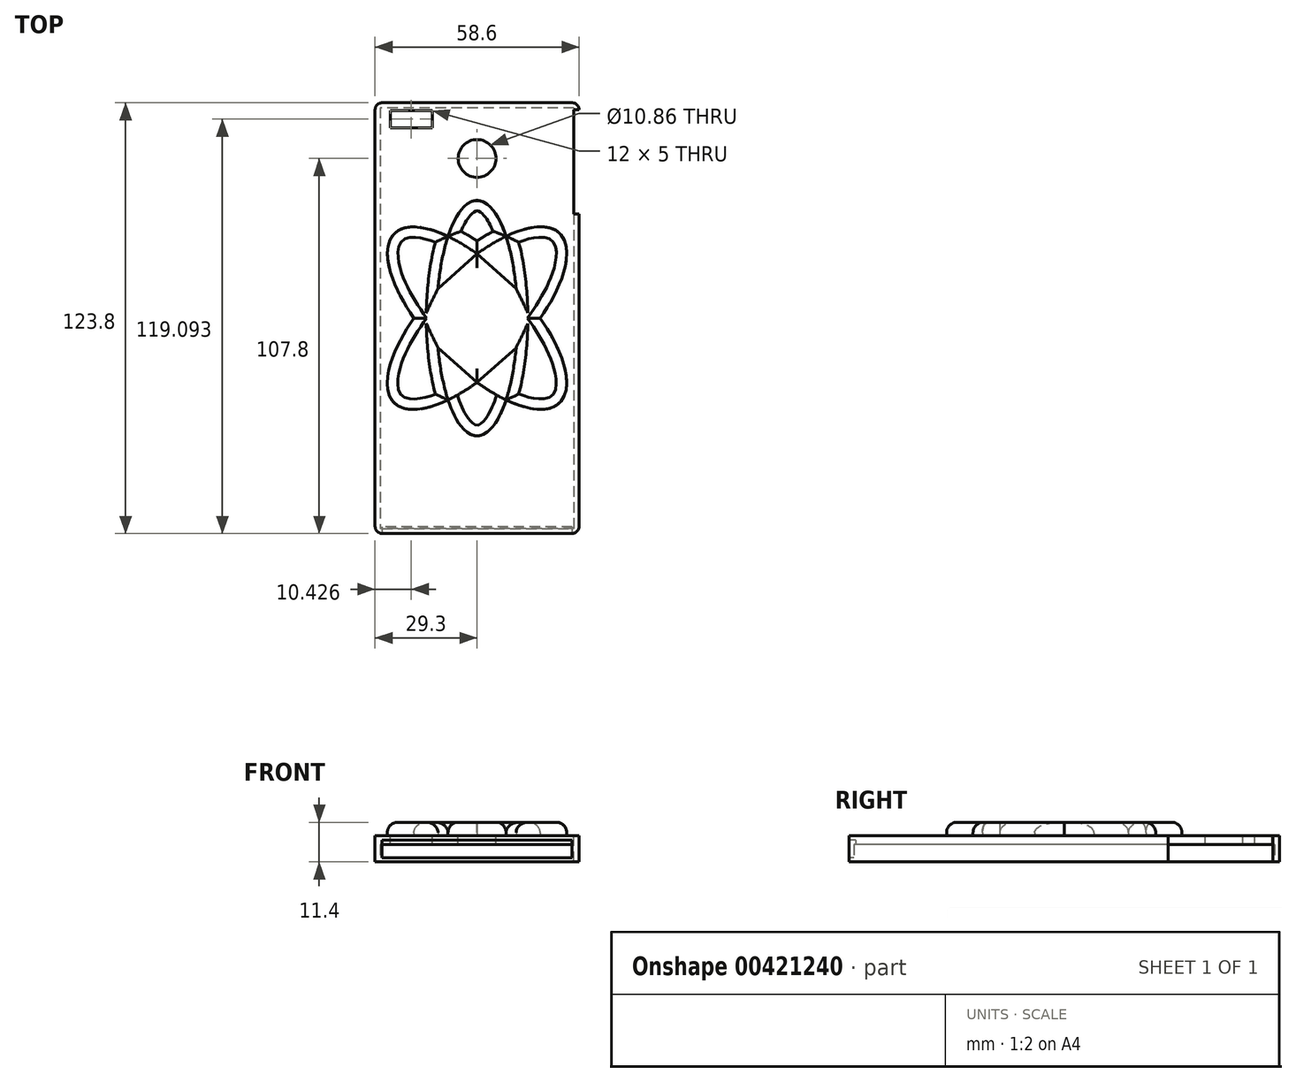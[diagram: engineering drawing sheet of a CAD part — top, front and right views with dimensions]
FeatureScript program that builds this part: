
annotation { "Feature Type Name" : "Feature", "Feature Type Description" : "" }
export const myFeature = defineFeature(function(context is Context, id is Id, definition is map)
    precondition{}
    {
        {
            var Q0;
            Q0=qCreatedBy(makeId("Top.planeOp"),FACE);
            var sketch = newSketch(context, id + "F0", { "sketchPlane" : qUnion([Q0])});
            skLineSegment(sketch, "E0", {"start": v(0, 0) * mm, "end": v(0, 69.75) * mm});
            skLineSegment(sketch, "E1", {"start": v(0, 0) * mm, "end": v(0, -69.75) * mm});
            skLineSegment(sketch, "E2", {"start": v(0, 0) * mm, "end": v(-58.6, 0) * mm});
            skLineSegment(sketch, "E3", {"start": v(0, 0) * mm, "end": v(70.03, 0) * mm});
            skLineSegment(sketch, "E4", {"start": v(70.03, 0) * mm, "end": v(70.03, 69.75) * mm});
            skLineSegment(sketch, "E5", {"start": v(0, 69.75) * mm, "end": v(70.03, 69.75) * mm});
            skLineSegment(sketch, "E6", {"start": v(70.03, 0) * mm, "end": v(70.03, -69.75) * mm});
            skLineSegment(sketch, "E7", {"start": v(70.03, -69.75) * mm, "end": v(0, -69.75) * mm});
            skLineSegment(sketch, "E8", {"start": v(0, -69.75) * mm, "end": v(-58.6, -69.75) * mm});
            skLineSegment(sketch, "E9", {"start": v(-58.6, -69.75) * mm, "end": v(-58.6, 0) * mm});
            skLineSegment(sketch, "E10", {"start": v(-58.6, 0) * mm, "end": v(-58.6, 69.75) * mm});
            skLineSegment(sketch, "E11", {"start": v(-58.6, 69.75) * mm, "end": v(0, 69.75) * mm});
            skLineSegment(sketch, "E12", {"start": v(-29.3, 0) * mm, "end": v(-29.3, 61.9) * mm});
            skLineSegment(sketch, "E13", {"start": v(-29.3, 0) * mm, "end": v(-29.3, -61.9) * mm});
            skLineSegment(sketch, "E14", {"start": v(-29.3, -61.9) * mm, "end": v(0, -61.9) * mm});
            skLineSegment(sketch, "E15", {"start": v(0, -61.9) * mm, "end": v(29.3, -61.9) * mm});
            skLineSegment(sketch, "E16", {"start": v(29.3, -61.9) * mm, "end": v(29.3, 61.9) * mm});
            skLineSegment(sketch, "E17", {"start": v(29.3, 61.9) * mm, "end": v(-29.3, 61.9) * mm});
            skSolve(sketch);
        }
        {
            var Q0;
            {var subQ4=sQuery(id+"F0.wireOp",EDGE,"E13");Q0=makeQuery(id+"F0.imprint","IMPRINT",FACE,{"disambiguationData":[TD([[makeQuery(id+"F0.imprint","IMPRINT",EDGE,{"derivedFrom":subQ4}),1.0]])]});}
            var Q1;
            {var subQ3=sQuery(id+"F0.wireOp",EDGE,"E15");Q1=makeQuery(id+"F0.imprint","IMPRINT",FACE,{"disambiguationData":[TD([[makeQuery(id+"F0.imprint","IMPRINT",EDGE,{"derivedFrom":subQ3}),1.0]])]});}
            var Q2;
            {var subQ3=sQuery(id+"F0.wireOp",EDGE,"E17");var subQ5=sQuery(id+"F0.wireOp",EDGE,"E16");var subQ7=makeQuery(id+"F0.imprint","INTERSECT",VERTEX,{"derivedFrom":[subQ5,subQ3]});Q2=makeQuery(id+"F0.imprint","IMPRINT",FACE,{"disambiguationData":[TD([[makeQuery(id+"F0.imprint","IMPRINT",EDGE,{"disambiguationData":[TD([[subQ7,1.0]])],"derivedFrom":subQ5}),1.0]])]});}
            var Q3;
            {var subQ5=sQuery(id+"F0.wireOp",EDGE,"E12");Q3=makeQuery(id+"F0.imprint","IMPRINT",FACE,{"disambiguationData":[TD([[makeQuery(id+"F0.imprint","IMPRINT",EDGE,{"derivedFrom":subQ5}),-1.0]])]});}
            extrude(context, id + "F1", {"entities" : qUnion([Q0, Q1, Q2, Q3]), "depth" : 7.6 * mm});
        }
        {
            var Q0;
            Q0=makeQuery(id+"F1.opExtrude","CAP_FACE",FACE,{"disambiguationData":[OSD([sQuery(id+"F0.wireOp",EDGE,"E12"),sQuery(id+"F0.wireOp",EDGE,"E13"),sQuery(id+"F0.wireOp",EDGE,"E14"),sQuery(id+"F0.wireOp",EDGE,"E15"),sQuery(id+"F0.wireOp",EDGE,"E16"),sQuery(id+"F0.wireOp",EDGE,"E17")])],"isStart":false});
            var sketch = newSketch(context, id + "F2", { "sketchPlane" : qUnion([Q0])});
            skEllipticalArc(sketch, "E18", {});
            skEllipticalArc(sketch, "E19", {});
            skEllipticalArc(sketch, "E20", {});
            skCircle(sketch, "E21", {"center": v(0, 0) * mm, "radius": 7.5 * mm});
            skEllipticalArc(sketch, "E22.trimOffspring", {});
            skEllipticalArc(sketch, "E23.trimOffspring", {});
            skEllipticalArc(sketch, "E24.trimOffspring", {});
            skLineSegment(sketch, "E25", {"start": v(-11.22, -8.52) * mm, "end": v(0, -18.48) * mm});
            skLineSegment(sketch, "E26", {"start": v(0, -18.48) * mm, "end": v(11.22, -8.52) * mm});
            skLineSegment(sketch, "E27", {"start": v(11.22, 8.52) * mm, "end": v(0, 18.48) * mm});
            skLineSegment(sketch, "E28", {"start": v(-11.22, 8.52) * mm, "end": v(0, 18.48) * mm});
            const initialGuessF2  = {"E18": [0, 0, 0, -1, 0.033824213712022835, 0.011594243973014003, 1.8254209141476943, 4.457725620937733], "E19": [0, 0, 0.6979285573378743, -0.7161673888500327, 0.033978122960102525, 0.014, 1.9707757385940963, 4.661466257985254], "E20": [0, 0, -0.6982818711147384, -0.715822903009187, 0.03404744300772042, 0.014, 4.763381791822066, 1.1718528018775047], "E22.trimOffspring": [0, 0, -0.6982818711147384, -0.715822903009187, 0.03404744300772042, 0.014, 1.6217891382322727, 4.313445455467297], "E23.trimOffspring": [0, 0, 0.6979285573378743, -0.7161673888500327, 0.033978122960102525, 0.014, 5.11236839218389, 1.5198736043954613], "E24.trimOffspring": [0, 0, 0, -1, 0.033824213712022835, 0.011594243973014003, 4.967013567737488, 1.3161329673479398]};
            skSetInitialGuess(sketch, initialGuessF2);
            skSolve(sketch);
        }
        {
            var Q0;
            {var subQ0=sQuery(id+"F2.wireOp",EDGE,"E24.trimOffspring");var subQ1=sQuery(id+"F2.wireOp",EDGE,"E20");var subQ2=makeQuery(id+"F2.imprint","INTERSECT",VERTEX,{"derivedFrom":[subQ1,subQ0]});Q0=makeQuery(id+"F2.imprint","IMPRINT",FACE,{"disambiguationData":[TD([[makeQuery(id+"F2.imprint","IMPRINT",EDGE,{"disambiguationData":[TD([[subQ2,-1.0]])],"derivedFrom":subQ0}),1.0]])]});}
            var Q1;
            {var subQ0=sQuery(id+"F2.wireOp",EDGE,"E22.trimOffspring");var subQ1=sQuery(id+"F2.wireOp",EDGE,"E18");var subQ2=makeQuery(id+"F2.imprint","INTERSECT",VERTEX,{"derivedFrom":[subQ1,subQ0]});Q1=makeQuery(id+"F2.imprint","IMPRINT",FACE,{"disambiguationData":[TD([[makeQuery(id+"F2.imprint","IMPRINT",EDGE,{"disambiguationData":[TD([[subQ2,-1.0]])],"derivedFrom":subQ1}),1.0]])]});}
            var Q2;
            {var subQ0=sQuery(id+"F2.wireOp",EDGE,"E23.trimOffspring");var subQ3=sQuery(id+"F2.wireOp",EDGE,"E22.trimOffspring");var subQ5=makeQuery(id+"F2.imprint","INTERSECT",VERTEX,{"derivedFrom":[subQ3,subQ0]});Q2=makeQuery(id+"F2.imprint","IMPRINT",FACE,{"disambiguationData":[TD([[makeQuery(id+"F2.imprint","IMPRINT",EDGE,{"disambiguationData":[TD([[subQ5,-1.0]])],"derivedFrom":subQ3}),1.0]])]});}
            var Q3;
            {var subQ1=sQuery(id+"F2.wireOp",EDGE,"E22.trimOffspring");var subQ3=sQuery(id+"F2.wireOp",EDGE,"E23.trimOffspring");var subQ4=makeQuery(id+"F2.imprint","INTERSECT",VERTEX,{"derivedFrom":[subQ1,subQ3]});Q3=makeQuery(id+"F2.imprint","IMPRINT",FACE,{"disambiguationData":[TD([[makeQuery(id+"F2.imprint","IMPRINT",EDGE,{"disambiguationData":[TD([[subQ4,1.0]])],"derivedFrom":subQ3}),1.0]])]});}
            var Q4;
            {var subQ1=sQuery(id+"F2.wireOp",EDGE,"E18");var subQ3=sQuery(id+"F2.wireOp",EDGE,"E19");var subQ4=makeQuery(id+"F2.imprint","INTERSECT",VERTEX,{"derivedFrom":[subQ1,subQ3]});Q4=makeQuery(id+"F2.imprint","IMPRINT",FACE,{"disambiguationData":[TD([[makeQuery(id+"F2.imprint","IMPRINT",EDGE,{"disambiguationData":[TD([[subQ4,-1.0]])],"derivedFrom":subQ3}),1.0]])]});}
            var Q5;
            {var subQ0=sQuery(id+"F2.wireOp",EDGE,"E24.trimOffspring");var subQ3=sQuery(id+"F2.wireOp",EDGE,"E20");var subQ5=makeQuery(id+"F2.imprint","INTERSECT",VERTEX,{"derivedFrom":[subQ3,subQ0]});Q5=makeQuery(id+"F2.imprint","IMPRINT",FACE,{"disambiguationData":[TD([[makeQuery(id+"F2.imprint","IMPRINT",EDGE,{"disambiguationData":[TD([[subQ5,1.0]])],"derivedFrom":subQ3}),1.0]])]});}
            var Q6;
            Q6=makeQuery(id+"F2.imprint","IMPRINT",FACE,{"disambiguationData":[TD([[makeQuery(id+"F2.imprint","IMPRINT",EDGE,{"derivedFrom":sQuery(id+"F2.wireOp",EDGE,"E21")}),-1.0]])]});
            var Q7;
            Q7=makeQuery(id+"F2.imprint","IMPRINT",FACE,{"disambiguationData":[TD([[makeQuery(id+"F2.imprint","IMPRINT",EDGE,{"derivedFrom":sQuery(id+"F2.wireOp",EDGE,"E21")}),1.0]])]});
            extrude(context, id + "F3", {"entities" : qUnion([Q0, Q1, Q2, Q3, Q4, Q5, Q6, Q7]), "depth" : 3.8 * mm});
        }
        {
            var Q0;
            Q0=makeQuery(id+"F3.opExtrude","CAP_EDGE",EDGE,{"disambiguationData":[OSD([sQuery(id+"F2.wireOp",EDGE,"E21")])],"isStart":false});
            var Q1;
            {var subQ0=sQuery(id+"F2.wireOp",EDGE,"E19");Q1=makeQuery(id+"F3.opExtrude","CAP_EDGE",EDGE,{"disambiguationData":[OSD([subQ0]),TDD([makeQuery(id+"F2.imprint","IMPRINT",EDGE,{"disambiguationData":[TD([[makeQuery(id+"F2.imprint","INTERSECT",VERTEX,{"derivedFrom":[sQuery(id+"F2.wireOp",EDGE,"E18"),subQ0]}),-1.0]])],"derivedFrom":subQ0})])],"isStart":false});}
            var Q2;
            {var subQ0=sQuery(id+"F2.wireOp",EDGE,"E22.trimOffspring");Q2=makeQuery(id+"F3.opExtrude","CAP_EDGE",EDGE,{"disambiguationData":[OSD([subQ0]),TDD([makeQuery(id+"F2.imprint","IMPRINT",EDGE,{"disambiguationData":[TD([[makeQuery(id+"F2.imprint","INTERSECT",VERTEX,{"derivedFrom":[subQ0,sQuery(id+"F2.wireOp",EDGE,"E23.trimOffspring")]}),-1.0]])],"derivedFrom":subQ0})])],"isStart":false});}
            var Q3;
            {var subQ0=sQuery(id+"F2.wireOp",EDGE,"E23.trimOffspring");Q3=makeQuery(id+"F3.opExtrude","CAP_EDGE",EDGE,{"disambiguationData":[OSD([subQ0]),TDD([makeQuery(id+"F2.imprint","IMPRINT",EDGE,{"disambiguationData":[TD([[makeQuery(id+"F2.imprint","INTERSECT",VERTEX,{"derivedFrom":[sQuery(id+"F2.wireOp",EDGE,"E22.trimOffspring"),subQ0]}),1.0]])],"derivedFrom":subQ0})])],"isStart":false});}
            var Q4;
            {var subQ0=sQuery(id+"F2.wireOp",EDGE,"E20");Q4=makeQuery(id+"F3.opExtrude","CAP_EDGE",EDGE,{"disambiguationData":[OSD([subQ0]),TDD([makeQuery(id+"F2.imprint","IMPRINT",EDGE,{"disambiguationData":[TD([[makeQuery(id+"F2.imprint","INTERSECT",VERTEX,{"derivedFrom":[subQ0,sQuery(id+"F2.wireOp",EDGE,"E24.trimOffspring")]}),1.0]])],"derivedFrom":subQ0})])],"isStart":false});}
            var Q5;
            Q5=makeQuery(id+"F3.opExtrude","CAP_FACE",FACE,{"disambiguationData":[OSD([sQuery(id+"F2.wireOp",EDGE,"E19"),sQuery(id+"F2.wireOp",EDGE,"E20"),sQuery(id+"F2.wireOp",EDGE,"E22.trimOffspring"),sQuery(id+"F2.wireOp",EDGE,"E23.trimOffspring"),sQuery(id+"F2.wireOp",EDGE,"E24.trimOffspring"),sQuery(id+"F2.wireOp",EDGE,"E25"),sQuery(id+"F2.wireOp",EDGE,"E26")])],"isStart":false});
            var Q6;
            Q6=makeQuery(id+"F3.opExtrude","CAP_FACE",FACE,{"disambiguationData":[OSD([sQuery(id+"F2.wireOp",EDGE,"E18"),sQuery(id+"F2.wireOp",EDGE,"E19"),sQuery(id+"F2.wireOp",EDGE,"E20"),sQuery(id+"F2.wireOp",EDGE,"E22.trimOffspring"),sQuery(id+"F2.wireOp",EDGE,"E23.trimOffspring"),sQuery(id+"F2.wireOp",EDGE,"E27"),sQuery(id+"F2.wireOp",EDGE,"E28")])],"isStart":false});
            var Q7;
            {var subQ0=sQuery(id+"F2.wireOp",EDGE,"E22.trimOffspring");Q7=makeQuery(id+"F3.opExtrude","CAP_EDGE",EDGE,{"disambiguationData":[OSD([subQ0]),TDD([makeQuery(id+"F2.imprint","IMPRINT",EDGE,{"disambiguationData":[TD([[makeQuery(id+"F2.imprint","INTERSECT",VERTEX,{"derivedFrom":[sQuery(id+"F2.wireOp",EDGE,"E18"),subQ0]}),-1.0]])],"derivedFrom":subQ0})])],"isStart":false});}
            var Q8;
            {var subQ0=sQuery(id+"F2.wireOp",EDGE,"E19");Q8=makeQuery(id+"F3.opExtrude","CAP_EDGE",EDGE,{"disambiguationData":[OSD([subQ0]),TDD([makeQuery(id+"F2.imprint","IMPRINT",EDGE,{"disambiguationData":[TD([[makeQuery(id+"F2.imprint","INTERSECT",VERTEX,{"derivedFrom":[sQuery(id+"F2.wireOp",EDGE,"E18"),subQ0]}),1.0]])],"derivedFrom":subQ0})])],"isStart":false});}
            var Q9;
            {var subQ0=sQuery(id+"F2.wireOp",EDGE,"E18");Q9=makeQuery(id+"F3.opExtrude","CAP_EDGE",EDGE,{"disambiguationData":[OSD([subQ0]),TDD([makeQuery(id+"F2.imprint","IMPRINT",EDGE,{"disambiguationData":[TD([[makeQuery(id+"F2.imprint","INTERSECT",VERTEX,{"derivedFrom":[subQ0,sQuery(id+"F2.wireOp",EDGE,"E22.trimOffspring")]}),-1.0]])],"derivedFrom":subQ0})])],"isStart":false});}
            var Q10;
            {var subQ0=sQuery(id+"F2.wireOp",EDGE,"E24.trimOffspring");Q10=makeQuery(id+"F3.opExtrude","CAP_EDGE",EDGE,{"disambiguationData":[OSD([subQ0]),TDD([makeQuery(id+"F2.imprint","IMPRINT",EDGE,{"disambiguationData":[TD([[makeQuery(id+"F2.imprint","INTERSECT",VERTEX,{"derivedFrom":[sQuery(id+"F2.wireOp",EDGE,"E20"),subQ0]}),-1.0]])],"derivedFrom":subQ0})])],"isStart":false});}
            fillet(context, id + "F4", {"entities" : qUnion([Q0, Q1, Q2, Q3, Q4, Q5, Q6, Q7, Q8, Q9, Q10]), "radius" : 3 * mm, "tangentPropagation" : true, "allowEdgeOverflow" : false});
        }
        {
            var Q0;
            Q0=makeQuery(id+"F1.opExtrude","CAP_FACE",FACE,{"disambiguationData":[OSD([sQuery(id+"F0.wireOp",EDGE,"E12"),sQuery(id+"F0.wireOp",EDGE,"E13"),sQuery(id+"F0.wireOp",EDGE,"E14"),sQuery(id+"F0.wireOp",EDGE,"E15"),sQuery(id+"F0.wireOp",EDGE,"E16"),sQuery(id+"F0.wireOp",EDGE,"E17")])],"isStart":false});
            var sketch = newSketch(context, id + "F5", { "sketchPlane" : qUnion([Q0])});
            skLineSegment(sketch, "E29", {"start": v(0, 0) * mm, "end": v(0, 61.9) * mm});
            skCircle(sketch, "E30", {"center": v(0, 45.9) * mm, "radius": 5.43 * mm});
            skLineSegment(sketch, "E31", {"start": v(-24.87, 54.7) * mm, "end": v(-12.87, 54.7) * mm});
            skLineSegment(sketch, "E32", {"start": v(-12.87, 54.7) * mm, "end": v(-12.87, 59.7) * mm});
            skLineSegment(sketch, "E33", {"start": v(-12.87, 59.7) * mm, "end": v(-24.87, 59.7) * mm});
            skLineSegment(sketch, "E34", {"start": v(-24.87, 59.7) * mm, "end": v(-24.87, 54.7) * mm});
            skSolve(sketch);
        }
        {
            var Q0;
            Q0=makeQuery(id+"F1.opExtrude","CAP_FACE",FACE,{"disambiguationData":[OSD([sQuery(id+"F0.wireOp",EDGE,"E12"),sQuery(id+"F0.wireOp",EDGE,"E13"),sQuery(id+"F0.wireOp",EDGE,"E14"),sQuery(id+"F0.wireOp",EDGE,"E15"),sQuery(id+"F0.wireOp",EDGE,"E16"),sQuery(id+"F0.wireOp",EDGE,"E17")])],"isStart":true});
            var sketch = newSketch(context, id + "F6", { "sketchPlane" : qUnion([Q0])});
            skLineSegment(sketch, "E35.bottom", {"start": v(27.84, -60.44) * mm, "end": v(-27.84, -60.44) * mm});
            skLineSegment(sketch, "E35.top", {"start": v(27.84, 60.44) * mm, "end": v(-27.84, 60.44) * mm});
            skLineSegment(sketch, "E35.left", {"start": v(27.84, -60.44) * mm, "end": v(27.84, 60.44) * mm});
            skLineSegment(sketch, "E35.right", {"start": v(-27.84, -60.44) * mm, "end": v(-27.84, 60.44) * mm});
            skSolve(sketch);
        }
        {
            var Q0;
            Q0=makeQuery(id+"F6.imprint","IMPRINT",FACE,{"disambiguationData":[TD([[makeQuery(id+"F6.imprint","IMPRINT",EDGE,{"derivedFrom":sQuery(id+"F6.wireOp",EDGE,"E35.bottom")}),-1.0]])]});
            extrude(context, id + "F7", {"entities" : qUnion([Q0]), "operationType" : NewBodyOperationType.REMOVE, "oppositeDirection" : true, "depth" : 5 * mm});
        }
        {
            var Q0;
            Q0=makeQuery(id+"F1.opExtrude","SWEPT_EDGE",EDGE,{"disambiguationData":[OSD([sQuery(id+"F0.wireOp",EDGE,"E16"),sQuery(id+"F0.wireOp",EDGE,"E17")])]});
            var Q1;
            Q1=makeQuery(id+"F1.opExtrude","SWEPT_EDGE",EDGE,{"disambiguationData":[OSD([sQuery(id+"F0.wireOp",EDGE,"E12"),sQuery(id+"F0.wireOp",EDGE,"E17")])]});
            var Q2;
            Q2=makeQuery(id+"F1.opExtrude","SWEPT_EDGE",EDGE,{"disambiguationData":[OSD([sQuery(id+"F0.wireOp",EDGE,"E13"),sQuery(id+"F0.wireOp",EDGE,"E14")])]});
            var Q3;
            Q3=makeQuery(id+"F1.opExtrude","SWEPT_EDGE",EDGE,{"disambiguationData":[OSD([sQuery(id+"F0.wireOp",EDGE,"E15"),sQuery(id+"F0.wireOp",EDGE,"E16")])]});
            fillet(context, id + "F8", {"entities" : qUnion([Q0, Q1, Q2, Q3]), "radius" : 2 * mm, "tangentPropagation" : true, "allowEdgeOverflow" : false});
        }
        {
            var Q0;
            {var subQ0=sQuery(id+"F5.wireOp",EDGE,"E30");var subQ1=sQuery(id+"F5.wireOp",EDGE,"E29");var subQ2=makeQuery(id+"F5.imprint","INTERSECT",VERTEX,{"disambiguationData":[OD(0.0)],"derivedFrom":[subQ1,subQ0]});Q0=makeQuery(id+"F5.imprint","IMPRINT",FACE,{"disambiguationData":[TD([[makeQuery(id+"F5.imprint","IMPRINT",EDGE,{"disambiguationData":[TD([[subQ2,-1.0]])],"derivedFrom":subQ1}),-1.0]])]});}
            var Q1;
            {var subQ0=sQuery(id+"F5.wireOp",EDGE,"E30");var subQ1=sQuery(id+"F5.wireOp",EDGE,"E29");var subQ2=makeQuery(id+"F5.imprint","INTERSECT",VERTEX,{"disambiguationData":[OD(0.0)],"derivedFrom":[subQ1,subQ0]});Q1=makeQuery(id+"F5.imprint","IMPRINT",FACE,{"disambiguationData":[TD([[makeQuery(id+"F5.imprint","IMPRINT",EDGE,{"disambiguationData":[TD([[subQ2,-1.0]])],"derivedFrom":subQ1}),1.0]])]});}
            extrude(context, id + "F9", {"entities" : qUnion([Q0, Q1]), "operationType" : NewBodyOperationType.REMOVE, "oppositeDirection" : true, "depth" : 25 * mm});
        }
        {
            var Q0;
            Q0 = qSketchRegion(id + "F5", true);
            extrude(context, id + "F10", {"entities" : qUnion([Q0]), "operationType" : NewBodyOperationType.REMOVE, "oppositeDirection" : true, "depth" : 25 * mm});
        }
        {
            var Q0;
            Q0=makeQuery(id+"F1.opExtrude","SWEPT_FACE",FACE,{"disambiguationData":[OSD([sQuery(id+"F0.wireOp",EDGE,"E14"),sQuery(id+"F0.wireOp",EDGE,"E15")])]});
            var sketch = newSketch(context, id + "F11", { "sketchPlane" : qUnion([Q0])});
            skLineSegment(sketch, "E36", {"start": v(-27.3, 6.22) * mm, "end": v(27.3, 6.22) * mm});
            skLineSegment(sketch, "E37", {"start": v(-27.3, 1.23) * mm, "end": v(27.3, 1.23) * mm});
            skSolve(sketch);
        }
        {
            var Q0;
            Q0 = qSketchRegion(id + "F11", true);
            var Q1;
            {var subQ0=sQuery(id+"F11.wireOp",EDGE,"E36");Q1=makeQuery(id+"F11.imprint","IMPRINT",FACE,{"disambiguationData":[TD([[makeQuery(id+"F11.imprint","IMPRINT",EDGE,{"derivedFrom":subQ0}),-1.0]])]});}
            extrude(context, id + "F12", {"entities" : qUnion([Q0, Q1]), "operationType" : NewBodyOperationType.REMOVE, "oppositeDirection" : true, "depth" : 1.9 * mm});
        }
        {
            var Q0;
            Q0=makeQuery(id+"F1.opExtrude","SWEPT_FACE",FACE,{"disambiguationData":[OSD([sQuery(id+"F0.wireOp",EDGE,"E16")])]});
            var sketch = newSketch(context, id + "F13", { "sketchPlane" : qUnion([Q0])});
            skLineSegment(sketch, "E38", {"start": v(59.9, 0) * mm, "end": v(59.9, 7.6) * mm});
            skLineSegment(sketch, "E39", {"start": v(29.9, 0) * mm, "end": v(29.9, 7.6) * mm});
            skSolve(sketch);
        }
        {
            var Q0;
            Q0 = qSketchRegion(id + "F13", true);
            var Q1;
            {var subQ0=sQuery(id+"F13.wireOp",EDGE,"E38");Q1=makeQuery(id+"F13.imprint","IMPRINT",FACE,{"disambiguationData":[TD([[makeQuery(id+"F13.imprint","IMPRINT",EDGE,{"derivedFrom":subQ0}),1.0]])]});}
            extrude(context, id + "F14", {"entities" : qUnion([Q0, Q1]), "operationType" : NewBodyOperationType.REMOVE, "oppositeDirection" : true, "depth" : 1.5 * mm});
        }
    });
